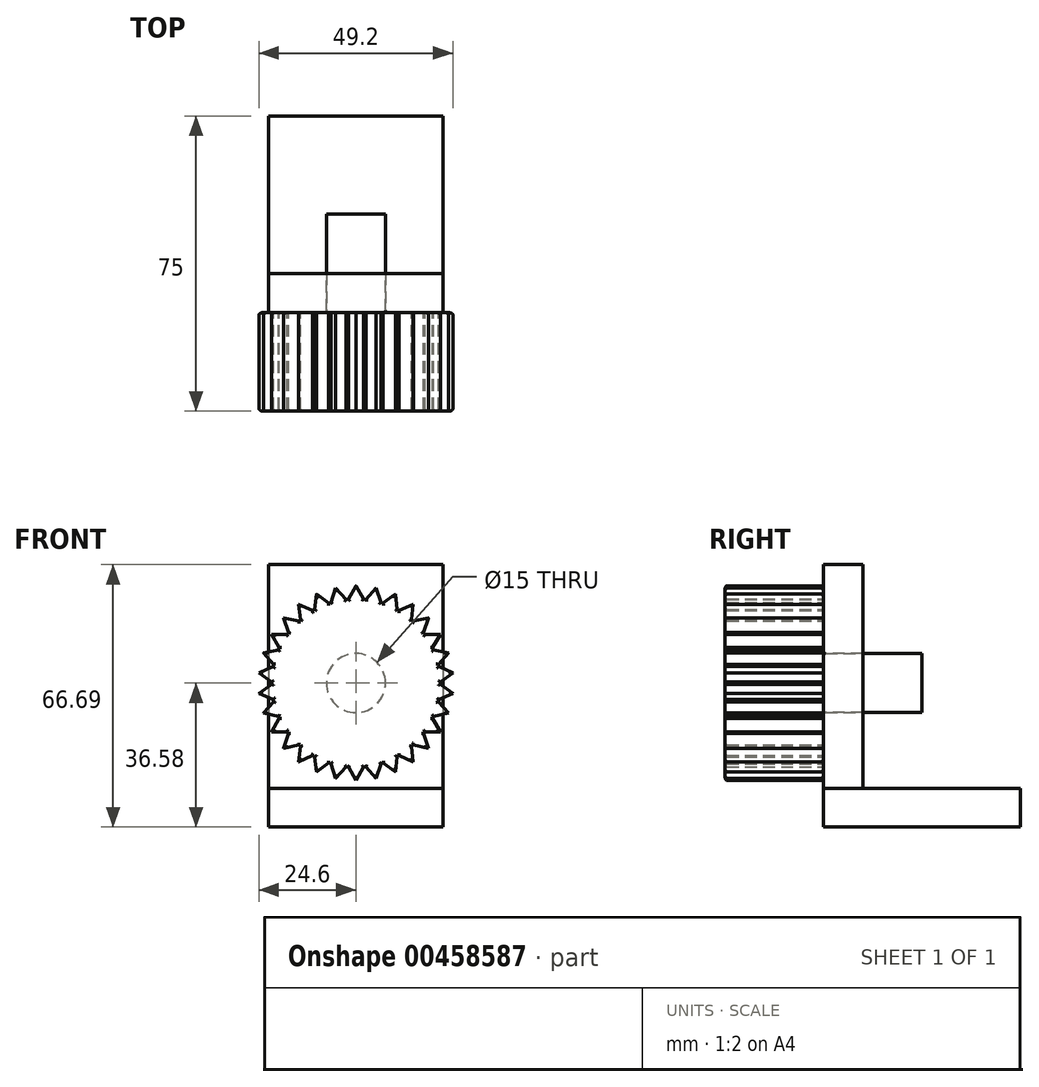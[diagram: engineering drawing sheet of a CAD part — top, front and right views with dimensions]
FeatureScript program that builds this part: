
annotation { "Feature Type Name" : "Feature", "Feature Type Description" : "" }
export const myFeature = defineFeature(function(context is Context, id is Id, definition is map)
    precondition{}
    {
        {
            var Q0;
            Q0=qCreatedBy(makeId("Front.planeOp"),FACE);
            var sketch = newSketch(context, id + "F0", { "sketchPlane" : qUnion([Q0])});
            skLineSegment(sketch, "E0.1", {"start": v(-1.94, 21.37) * mm, "end": v(0, 24.73) * mm});
            skLineSegment(sketch, "E0.2", {"start": v(0, 24.73) * mm, "end": v(1.94, 21.37) * mm});
            skLineSegment(sketch, "E1.1.0", {"start": v(-5.14, 24.2) * mm, "end": v(-2.54, 21.3) * mm});
            skLineSegment(sketch, "E1.1.1", {"start": v(-6.34, 20.5) * mm, "end": v(-5.14, 24.2) * mm});
            skLineSegment(sketch, "E1.2.0", {"start": v(-10.06, 22.6) * mm, "end": v(-6.91, 20.3) * mm});
            skLineSegment(sketch, "E1.2.1", {"start": v(-10.47, 18.73) * mm, "end": v(-10.06, 22.6) * mm});
            skPoint(sketch, "E1.center", {"position": v(0, 0) * mm});
            skLineSegment(sketch, "E2.3.3.0", {"start": v(-14.13, 16.14) * mm, "end": v(-14.54, 20.01) * mm});
            skLineSegment(sketch, "E2.4.3.0", {"start": v(-14.54, 20.01) * mm, "end": v(-10.99, 18.43) * mm});
            skLineSegment(sketch, "E2.3.4.0", {"start": v(-17.18, 12.85) * mm, "end": v(-18.38, 16.55) * mm});
            skLineSegment(sketch, "E2.4.4.0", {"start": v(-18.38, 16.55) * mm, "end": v(-14.58, 15.74) * mm});
            skLineSegment(sketch, "E2.3.5.0", {"start": v(-19.48, 9) * mm, "end": v(-21.42, 12.37) * mm});
            skLineSegment(sketch, "E2.4.5.0", {"start": v(-21.42, 12.37) * mm, "end": v(-17.53, 12.37) * mm});
            skLineSegment(sketch, "E2.3.6.0", {"start": v(-20.92, 4.75) * mm, "end": v(-23.52, 7.64) * mm});
            skLineSegment(sketch, "E2.4.6.0", {"start": v(-23.52, 7.64) * mm, "end": v(-19.72, 8.45) * mm});
            skLineSegment(sketch, "E2.3.7.0", {"start": v(-21.45, 0.3) * mm, "end": v(-24.6, 2.59) * mm});
            skLineSegment(sketch, "E2.4.7.0", {"start": v(-24.6, 2.59) * mm, "end": v(-21.05, 4.17) * mm});
            skLineSegment(sketch, "E2.3.8.0", {"start": v(-21.05, -4.17) * mm, "end": v(-24.6, -2.59) * mm});
            skLineSegment(sketch, "E2.4.8.0", {"start": v(-24.6, -2.59) * mm, "end": v(-21.45, -0.3) * mm});
            skLineSegment(sketch, "E2.3.9.0", {"start": v(-19.72, -8.45) * mm, "end": v(-23.52, -7.64) * mm});
            skLineSegment(sketch, "E2.4.9.0", {"start": v(-23.52, -7.64) * mm, "end": v(-20.92, -4.75) * mm});
            skLineSegment(sketch, "E2.3.10.0", {"start": v(-17.53, -12.37) * mm, "end": v(-21.42, -12.37) * mm});
            skLineSegment(sketch, "E2.4.10.0", {"start": v(-21.42, -12.37) * mm, "end": v(-19.48, -9) * mm});
            skLineSegment(sketch, "E2.3.11.0", {"start": v(-14.58, -15.74) * mm, "end": v(-18.38, -16.55) * mm});
            skLineSegment(sketch, "E2.4.11.0", {"start": v(-18.38, -16.55) * mm, "end": v(-17.18, -12.85) * mm});
            skLineSegment(sketch, "E2.3.12.0", {"start": v(-10.99, -18.43) * mm, "end": v(-14.54, -20.01) * mm});
            skLineSegment(sketch, "E2.4.12.0", {"start": v(-14.54, -20.01) * mm, "end": v(-14.13, -16.14) * mm});
            skLineSegment(sketch, "E2.3.13.0", {"start": v(-6.91, -20.3) * mm, "end": v(-10.06, -22.6) * mm});
            skLineSegment(sketch, "E2.4.13.0", {"start": v(-10.06, -22.6) * mm, "end": v(-10.47, -18.73) * mm});
            skLineSegment(sketch, "E2.3.14.0", {"start": v(-2.54, -21.3) * mm, "end": v(-5.14, -24.2) * mm});
            skLineSegment(sketch, "E2.4.14.0", {"start": v(-5.14, -24.2) * mm, "end": v(-6.34, -20.5) * mm});
            skLineSegment(sketch, "E2.3.15.0", {"start": v(1.94, -21.37) * mm, "end": v(0, -24.73) * mm});
            skLineSegment(sketch, "E2.4.15.0", {"start": v(0, -24.73) * mm, "end": v(-1.94, -21.37) * mm});
            skLineSegment(sketch, "E2.3.16.0", {"start": v(6.34, -20.5) * mm, "end": v(5.14, -24.2) * mm});
            skLineSegment(sketch, "E2.4.16.0", {"start": v(5.14, -24.2) * mm, "end": v(2.54, -21.3) * mm});
            skLineSegment(sketch, "E2.3.17.0", {"start": v(10.47, -18.73) * mm, "end": v(10.06, -22.6) * mm});
            skLineSegment(sketch, "E2.4.17.0", {"start": v(10.06, -22.6) * mm, "end": v(6.91, -20.3) * mm});
            skLineSegment(sketch, "E2.3.18.0", {"start": v(14.13, -16.14) * mm, "end": v(14.54, -20.01) * mm});
            skLineSegment(sketch, "E2.4.18.0", {"start": v(14.54, -20.01) * mm, "end": v(10.99, -18.43) * mm});
            skLineSegment(sketch, "E2.3.19.0", {"start": v(17.18, -12.85) * mm, "end": v(18.38, -16.55) * mm});
            skLineSegment(sketch, "E2.4.19.0", {"start": v(18.38, -16.55) * mm, "end": v(14.58, -15.74) * mm});
            skLineSegment(sketch, "E2.3.20.0", {"start": v(19.48, -9) * mm, "end": v(21.42, -12.37) * mm});
            skLineSegment(sketch, "E2.4.20.0", {"start": v(21.42, -12.37) * mm, "end": v(17.53, -12.37) * mm});
            skLineSegment(sketch, "E2.3.21.0", {"start": v(20.92, -4.75) * mm, "end": v(23.52, -7.64) * mm});
            skLineSegment(sketch, "E2.4.21.0", {"start": v(23.52, -7.64) * mm, "end": v(19.72, -8.45) * mm});
            skLineSegment(sketch, "E2.3.22.0", {"start": v(21.45, -0.3) * mm, "end": v(24.6, -2.59) * mm});
            skLineSegment(sketch, "E2.4.22.0", {"start": v(24.6, -2.59) * mm, "end": v(21.05, -4.17) * mm});
            skLineSegment(sketch, "E2.3.23.0", {"start": v(21.05, 4.17) * mm, "end": v(24.6, 2.59) * mm});
            skLineSegment(sketch, "E2.4.23.0", {"start": v(24.6, 2.59) * mm, "end": v(21.45, 0.3) * mm});
            skLineSegment(sketch, "E2.3.24.0", {"start": v(19.72, 8.45) * mm, "end": v(23.52, 7.64) * mm});
            skLineSegment(sketch, "E2.4.24.0", {"start": v(23.52, 7.64) * mm, "end": v(20.92, 4.75) * mm});
            skLineSegment(sketch, "E2.3.25.0", {"start": v(17.53, 12.37) * mm, "end": v(21.42, 12.37) * mm});
            skLineSegment(sketch, "E2.4.25.0", {"start": v(21.42, 12.37) * mm, "end": v(19.48, 9) * mm});
            skLineSegment(sketch, "E2.3.26.0", {"start": v(14.58, 15.74) * mm, "end": v(18.38, 16.55) * mm});
            skLineSegment(sketch, "E2.4.26.0", {"start": v(18.38, 16.55) * mm, "end": v(17.18, 12.85) * mm});
            skLineSegment(sketch, "E2.3.27.0", {"start": v(10.99, 18.43) * mm, "end": v(14.54, 20.01) * mm});
            skLineSegment(sketch, "E2.4.27.0", {"start": v(14.54, 20.01) * mm, "end": v(14.13, 16.14) * mm});
            skLineSegment(sketch, "E2.3.28.0", {"start": v(6.91, 20.3) * mm, "end": v(10.06, 22.6) * mm});
            skLineSegment(sketch, "E2.4.28.0", {"start": v(10.06, 22.6) * mm, "end": v(10.47, 18.73) * mm});
            skLineSegment(sketch, "E2.3.29.0", {"start": v(2.54, 21.3) * mm, "end": v(5.14, 24.2) * mm});
            skLineSegment(sketch, "E2.4.29.0", {"start": v(5.14, 24.2) * mm, "end": v(6.34, 20.5) * mm});
            skLineSegment(sketch, "E3", {"start": v(-2.54, 21.3) * mm, "end": v(-1.94, 21.37) * mm});
            skLineSegment(sketch, "E4.1.0", {"start": v(-6.91, 20.3) * mm, "end": v(-6.34, 20.5) * mm});
            skLineSegment(sketch, "E4.2.0", {"start": v(-10.99, 18.43) * mm, "end": v(-10.47, 18.73) * mm});
            skLineSegment(sketch, "E4.3.0", {"start": v(-14.58, 15.74) * mm, "end": v(-14.13, 16.14) * mm});
            skLineSegment(sketch, "E4.4.0", {"start": v(-17.53, 12.37) * mm, "end": v(-17.18, 12.85) * mm});
            skLineSegment(sketch, "E4.5.0", {"start": v(-19.72, 8.45) * mm, "end": v(-19.48, 9) * mm});
            skLineSegment(sketch, "E4.6.0", {"start": v(-21.05, 4.17) * mm, "end": v(-20.92, 4.75) * mm});
            skLineSegment(sketch, "E4.7.0", {"start": v(-21.45, -0.3) * mm, "end": v(-21.45, 0.3) * mm});
            skLineSegment(sketch, "E4.8.0", {"start": v(-20.92, -4.75) * mm, "end": v(-21.05, -4.17) * mm});
            skLineSegment(sketch, "E4.9.0", {"start": v(-19.48, -9) * mm, "end": v(-19.72, -8.45) * mm});
            skLineSegment(sketch, "E4.10.0", {"start": v(-17.18, -12.85) * mm, "end": v(-17.53, -12.37) * mm});
            skLineSegment(sketch, "E4.11.0", {"start": v(-14.13, -16.14) * mm, "end": v(-14.58, -15.74) * mm});
            skLineSegment(sketch, "E4.12.0", {"start": v(-10.47, -18.73) * mm, "end": v(-10.99, -18.43) * mm});
            skLineSegment(sketch, "E4.13.0", {"start": v(-6.34, -20.5) * mm, "end": v(-6.91, -20.3) * mm});
            skLineSegment(sketch, "E4.14.0", {"start": v(-1.94, -21.37) * mm, "end": v(-2.54, -21.3) * mm});
            skLineSegment(sketch, "E4.15.0", {"start": v(2.54, -21.3) * mm, "end": v(1.94, -21.37) * mm});
            skLineSegment(sketch, "E4.16.0", {"start": v(6.91, -20.3) * mm, "end": v(6.34, -20.5) * mm});
            skLineSegment(sketch, "E4.17.0", {"start": v(10.99, -18.43) * mm, "end": v(10.47, -18.73) * mm});
            skLineSegment(sketch, "E4.18.0", {"start": v(14.58, -15.74) * mm, "end": v(14.13, -16.14) * mm});
            skLineSegment(sketch, "E4.19.0", {"start": v(17.53, -12.37) * mm, "end": v(17.18, -12.85) * mm});
            skLineSegment(sketch, "E4.20.0", {"start": v(19.72, -8.45) * mm, "end": v(19.48, -9) * mm});
            skLineSegment(sketch, "E4.21.0", {"start": v(21.05, -4.17) * mm, "end": v(20.92, -4.75) * mm});
            skLineSegment(sketch, "E4.22.0", {"start": v(21.45, 0.3) * mm, "end": v(21.45, -0.3) * mm});
            skLineSegment(sketch, "E4.23.0", {"start": v(20.92, 4.75) * mm, "end": v(21.05, 4.17) * mm});
            skLineSegment(sketch, "E4.24.0", {"start": v(19.48, 9) * mm, "end": v(19.72, 8.45) * mm});
            skLineSegment(sketch, "E4.25.0", {"start": v(17.18, 12.85) * mm, "end": v(17.53, 12.37) * mm});
            skLineSegment(sketch, "E4.26.0", {"start": v(14.13, 16.14) * mm, "end": v(14.58, 15.74) * mm});
            skLineSegment(sketch, "E4.27.0", {"start": v(10.47, 18.73) * mm, "end": v(10.99, 18.43) * mm});
            skLineSegment(sketch, "E4.28.0", {"start": v(6.34, 20.5) * mm, "end": v(6.91, 20.3) * mm});
            skLineSegment(sketch, "E4.29.0", {"start": v(1.94, 21.37) * mm, "end": v(2.54, 21.3) * mm});
            skCircle(sketch, "E5", {"center": v(0, 0) * mm, "radius": 7.5 * mm});
            skSolve(sketch);
        }
        {
            var Q0;
            Q0=makeQuery(id+"F0.imprint","IMPRINT",FACE,{"disambiguationData":[TD([[makeQuery(id+"F0.imprint","IMPRINT",EDGE,{"derivedFrom":sQuery(id+"F0.wireOp",EDGE,"E0.1")}),-1.0]])]});
            extrude(context, id + "F1", {"entities" : qUnion([Q0]), "depth" : 25 * mm});
        }
        {
            var Q0;
            Q0=makeQuery(id+"F0.imprint","IMPRINT",FACE,{"disambiguationData":[TD([[makeQuery(id+"F0.imprint","IMPRINT",EDGE,{"derivedFrom":sQuery(id+"F0.wireOp",EDGE,"E5")}),1.0]])]});
            extrude(context, id + "F2", {"entities" : qUnion([Q0]), "operationType" : NewBodyOperationType.ADD, "endBound" : BoundingType.SYMMETRIC, "depth" : 50 * mm});
        }
        {
            var Q0;
            {var subQ0=sQuery(id+"F0.wireOp",EDGE,"E5");Q0=makeQuery(id+"F2.boolean.opBoolean","MERGE",FACE,{"derivedFrom":[makeQuery(id+"F1.opExtrude","CAP_FACE",FACE,{"disambiguationData":[OSD([sQuery(id+"F0.wireOp",EDGE,"E0.1"),sQuery(id+"F0.wireOp",EDGE,"E0.2"),sQuery(id+"F0.wireOp",EDGE,"E1.1.0"),sQuery(id+"F0.wireOp",EDGE,"E1.1.1"),sQuery(id+"F0.wireOp",EDGE,"E1.2.0"),sQuery(id+"F0.wireOp",EDGE,"E1.2.1"),sQuery(id+"F0.wireOp",EDGE,"E2.3.3.0"),sQuery(id+"F0.wireOp",EDGE,"E2.4.3.0"),sQuery(id+"F0.wireOp",EDGE,"E2.3.4.0"),sQuery(id+"F0.wireOp",EDGE,"E2.4.4.0"),sQuery(id+"F0.wireOp",EDGE,"E2.3.5.0"),sQuery(id+"F0.wireOp",EDGE,"E2.4.5.0"),sQuery(id+"F0.wireOp",EDGE,"E2.3.6.0"),sQuery(id+"F0.wireOp",EDGE,"E2.4.6.0"),sQuery(id+"F0.wireOp",EDGE,"E2.3.7.0"),sQuery(id+"F0.wireOp",EDGE,"E2.4.7.0"),sQuery(id+"F0.wireOp",EDGE,"E2.3.8.0"),sQuery(id+"F0.wireOp",EDGE,"E2.4.8.0"),sQuery(id+"F0.wireOp",EDGE,"E2.3.9.0"),sQuery(id+"F0.wireOp",EDGE,"E2.4.9.0"),sQuery(id+"F0.wireOp",EDGE,"E2.3.10.0"),sQuery(id+"F0.wireOp",EDGE,"E2.4.10.0"),sQuery(id+"F0.wireOp",EDGE,"E2.3.11.0"),sQuery(id+"F0.wireOp",EDGE,"E2.4.11.0"),sQuery(id+"F0.wireOp",EDGE,"E2.3.12.0"),sQuery(id+"F0.wireOp",EDGE,"E2.4.12.0"),sQuery(id+"F0.wireOp",EDGE,"E2.3.13.0"),sQuery(id+"F0.wireOp",EDGE,"E2.4.13.0"),sQuery(id+"F0.wireOp",EDGE,"E2.3.14.0"),sQuery(id+"F0.wireOp",EDGE,"E2.4.14.0"),sQuery(id+"F0.wireOp",EDGE,"E2.3.15.0"),sQuery(id+"F0.wireOp",EDGE,"E2.4.15.0"),sQuery(id+"F0.wireOp",EDGE,"E2.3.16.0"),sQuery(id+"F0.wireOp",EDGE,"E2.4.16.0"),sQuery(id+"F0.wireOp",EDGE,"E2.3.17.0"),sQuery(id+"F0.wireOp",EDGE,"E2.4.17.0"),sQuery(id+"F0.wireOp",EDGE,"E2.3.18.0"),sQuery(id+"F0.wireOp",EDGE,"E2.4.18.0"),sQuery(id+"F0.wireOp",EDGE,"E2.3.19.0"),sQuery(id+"F0.wireOp",EDGE,"E2.4.19.0"),sQuery(id+"F0.wireOp",EDGE,"E2.3.20.0"),sQuery(id+"F0.wireOp",EDGE,"E2.4.20.0"),sQuery(id+"F0.wireOp",EDGE,"E2.3.21.0"),sQuery(id+"F0.wireOp",EDGE,"E2.4.21.0"),sQuery(id+"F0.wireOp",EDGE,"E2.3.22.0"),sQuery(id+"F0.wireOp",EDGE,"E2.4.22.0"),sQuery(id+"F0.wireOp",EDGE,"E2.3.23.0"),sQuery(id+"F0.wireOp",EDGE,"E2.4.23.0"),sQuery(id+"F0.wireOp",EDGE,"E2.3.24.0"),sQuery(id+"F0.wireOp",EDGE,"E2.4.24.0"),sQuery(id+"F0.wireOp",EDGE,"E2.3.25.0"),sQuery(id+"F0.wireOp",EDGE,"E2.4.25.0"),sQuery(id+"F0.wireOp",EDGE,"E2.3.26.0"),sQuery(id+"F0.wireOp",EDGE,"E2.4.26.0"),sQuery(id+"F0.wireOp",EDGE,"E2.3.27.0"),sQuery(id+"F0.wireOp",EDGE,"E2.4.27.0"),sQuery(id+"F0.wireOp",EDGE,"E2.3.28.0"),sQuery(id+"F0.wireOp",EDGE,"E2.4.28.0"),sQuery(id+"F0.wireOp",EDGE,"E2.3.29.0"),sQuery(id+"F0.wireOp",EDGE,"E2.4.29.0"),sQuery(id+"F0.wireOp",EDGE,"E3"),sQuery(id+"F0.wireOp",EDGE,"E4.1.0"),sQuery(id+"F0.wireOp",EDGE,"E4.2.0"),sQuery(id+"F0.wireOp",EDGE,"E4.3.0"),sQuery(id+"F0.wireOp",EDGE,"E4.4.0"),sQuery(id+"F0.wireOp",EDGE,"E4.5.0"),sQuery(id+"F0.wireOp",EDGE,"E4.6.0"),sQuery(id+"F0.wireOp",EDGE,"E4.7.0"),sQuery(id+"F0.wireOp",EDGE,"E4.8.0"),sQuery(id+"F0.wireOp",EDGE,"E4.9.0"),sQuery(id+"F0.wireOp",EDGE,"E4.10.0"),sQuery(id+"F0.wireOp",EDGE,"E4.11.0"),sQuery(id+"F0.wireOp",EDGE,"E4.12.0"),sQuery(id+"F0.wireOp",EDGE,"E4.13.0"),sQuery(id+"F0.wireOp",EDGE,"E4.14.0"),sQuery(id+"F0.wireOp",EDGE,"E4.15.0"),sQuery(id+"F0.wireOp",EDGE,"E4.16.0"),sQuery(id+"F0.wireOp",EDGE,"E4.17.0"),sQuery(id+"F0.wireOp",EDGE,"E4.18.0"),sQuery(id+"F0.wireOp",EDGE,"E4.19.0"),sQuery(id+"F0.wireOp",EDGE,"E4.20.0"),sQuery(id+"F0.wireOp",EDGE,"E4.21.0"),sQuery(id+"F0.wireOp",EDGE,"E4.22.0"),sQuery(id+"F0.wireOp",EDGE,"E4.23.0"),sQuery(id+"F0.wireOp",EDGE,"E4.24.0"),sQuery(id+"F0.wireOp",EDGE,"E4.25.0"),sQuery(id+"F0.wireOp",EDGE,"E4.26.0"),sQuery(id+"F0.wireOp",EDGE,"E4.27.0"),sQuery(id+"F0.wireOp",EDGE,"E4.28.0"),sQuery(id+"F0.wireOp",EDGE,"E4.29.0"),subQ0])],"isStart":false}),makeQuery(id+"F2.opExtrude","CAP_FACE",FACE,{"disambiguationData":[OSD([subQ0])],"isStart":false})]});}
            var Q1;
            Q1=makeQuery(id+"F1.opExtrude","CAP_EDGE",EDGE,{"disambiguationData":[OSD([sQuery(id+"F0.wireOp",EDGE,"E2.4.9.0")])],"isStart":false});
            fillet(context, id + "F3", {"entities" : qUnion([Q0, Q1]), "radius" : 0.5 * mm, "tangentPropagation" : true, "allowEdgeOverflow" : false});
        }
        {
            var Q0;
            Q0=makeQuery(id+"F1.opExtrude","CAP_EDGE",EDGE,{"disambiguationData":[OSD([sQuery(id+"F0.wireOp",EDGE,"E1.2.1")])],"isStart":true});
            var Q1;
            Q1=makeQuery(id+"F1.opExtrude","CAP_FACE",FACE,{"disambiguationData":[OSD([sQuery(id+"F0.wireOp",EDGE,"E0.1"),sQuery(id+"F0.wireOp",EDGE,"E0.2"),sQuery(id+"F0.wireOp",EDGE,"E1.1.0"),sQuery(id+"F0.wireOp",EDGE,"E1.1.1"),sQuery(id+"F0.wireOp",EDGE,"E1.2.0"),sQuery(id+"F0.wireOp",EDGE,"E1.2.1"),sQuery(id+"F0.wireOp",EDGE,"E2.3.3.0"),sQuery(id+"F0.wireOp",EDGE,"E2.4.3.0"),sQuery(id+"F0.wireOp",EDGE,"E2.3.4.0"),sQuery(id+"F0.wireOp",EDGE,"E2.4.4.0"),sQuery(id+"F0.wireOp",EDGE,"E2.3.5.0"),sQuery(id+"F0.wireOp",EDGE,"E2.4.5.0"),sQuery(id+"F0.wireOp",EDGE,"E2.3.6.0"),sQuery(id+"F0.wireOp",EDGE,"E2.4.6.0"),sQuery(id+"F0.wireOp",EDGE,"E2.3.7.0"),sQuery(id+"F0.wireOp",EDGE,"E2.4.7.0"),sQuery(id+"F0.wireOp",EDGE,"E2.3.8.0"),sQuery(id+"F0.wireOp",EDGE,"E2.4.8.0"),sQuery(id+"F0.wireOp",EDGE,"E2.3.9.0"),sQuery(id+"F0.wireOp",EDGE,"E2.4.9.0"),sQuery(id+"F0.wireOp",EDGE,"E2.3.10.0"),sQuery(id+"F0.wireOp",EDGE,"E2.4.10.0"),sQuery(id+"F0.wireOp",EDGE,"E2.3.11.0"),sQuery(id+"F0.wireOp",EDGE,"E2.4.11.0"),sQuery(id+"F0.wireOp",EDGE,"E2.3.12.0"),sQuery(id+"F0.wireOp",EDGE,"E2.4.12.0"),sQuery(id+"F0.wireOp",EDGE,"E2.3.13.0"),sQuery(id+"F0.wireOp",EDGE,"E2.4.13.0"),sQuery(id+"F0.wireOp",EDGE,"E2.3.14.0"),sQuery(id+"F0.wireOp",EDGE,"E2.4.14.0"),sQuery(id+"F0.wireOp",EDGE,"E2.3.15.0"),sQuery(id+"F0.wireOp",EDGE,"E2.4.15.0"),sQuery(id+"F0.wireOp",EDGE,"E2.3.16.0"),sQuery(id+"F0.wireOp",EDGE,"E2.4.16.0"),sQuery(id+"F0.wireOp",EDGE,"E2.3.17.0"),sQuery(id+"F0.wireOp",EDGE,"E2.4.17.0"),sQuery(id+"F0.wireOp",EDGE,"E2.3.18.0"),sQuery(id+"F0.wireOp",EDGE,"E2.4.18.0"),sQuery(id+"F0.wireOp",EDGE,"E2.3.19.0"),sQuery(id+"F0.wireOp",EDGE,"E2.4.19.0"),sQuery(id+"F0.wireOp",EDGE,"E2.3.20.0"),sQuery(id+"F0.wireOp",EDGE,"E2.4.20.0"),sQuery(id+"F0.wireOp",EDGE,"E2.3.21.0"),sQuery(id+"F0.wireOp",EDGE,"E2.4.21.0"),sQuery(id+"F0.wireOp",EDGE,"E2.3.22.0"),sQuery(id+"F0.wireOp",EDGE,"E2.4.22.0"),sQuery(id+"F0.wireOp",EDGE,"E2.3.23.0"),sQuery(id+"F0.wireOp",EDGE,"E2.4.23.0"),sQuery(id+"F0.wireOp",EDGE,"E2.3.24.0"),sQuery(id+"F0.wireOp",EDGE,"E2.4.24.0"),sQuery(id+"F0.wireOp",EDGE,"E2.3.25.0"),sQuery(id+"F0.wireOp",EDGE,"E2.4.25.0"),sQuery(id+"F0.wireOp",EDGE,"E2.3.26.0"),sQuery(id+"F0.wireOp",EDGE,"E2.4.26.0"),sQuery(id+"F0.wireOp",EDGE,"E2.3.27.0"),sQuery(id+"F0.wireOp",EDGE,"E2.4.27.0"),sQuery(id+"F0.wireOp",EDGE,"E2.3.28.0"),sQuery(id+"F0.wireOp",EDGE,"E2.4.28.0"),sQuery(id+"F0.wireOp",EDGE,"E2.3.29.0"),sQuery(id+"F0.wireOp",EDGE,"E2.4.29.0"),sQuery(id+"F0.wireOp",EDGE,"E3"),sQuery(id+"F0.wireOp",EDGE,"E4.1.0"),sQuery(id+"F0.wireOp",EDGE,"E4.2.0"),sQuery(id+"F0.wireOp",EDGE,"E4.3.0"),sQuery(id+"F0.wireOp",EDGE,"E4.4.0"),sQuery(id+"F0.wireOp",EDGE,"E4.5.0"),sQuery(id+"F0.wireOp",EDGE,"E4.6.0"),sQuery(id+"F0.wireOp",EDGE,"E4.7.0"),sQuery(id+"F0.wireOp",EDGE,"E4.8.0"),sQuery(id+"F0.wireOp",EDGE,"E4.9.0"),sQuery(id+"F0.wireOp",EDGE,"E4.10.0"),sQuery(id+"F0.wireOp",EDGE,"E4.11.0"),sQuery(id+"F0.wireOp",EDGE,"E4.12.0"),sQuery(id+"F0.wireOp",EDGE,"E4.13.0"),sQuery(id+"F0.wireOp",EDGE,"E4.14.0"),sQuery(id+"F0.wireOp",EDGE,"E4.15.0"),sQuery(id+"F0.wireOp",EDGE,"E4.16.0"),sQuery(id+"F0.wireOp",EDGE,"E4.17.0"),sQuery(id+"F0.wireOp",EDGE,"E4.18.0"),sQuery(id+"F0.wireOp",EDGE,"E4.19.0"),sQuery(id+"F0.wireOp",EDGE,"E4.20.0"),sQuery(id+"F0.wireOp",EDGE,"E4.21.0"),sQuery(id+"F0.wireOp",EDGE,"E4.22.0"),sQuery(id+"F0.wireOp",EDGE,"E4.23.0"),sQuery(id+"F0.wireOp",EDGE,"E4.24.0"),sQuery(id+"F0.wireOp",EDGE,"E4.25.0"),sQuery(id+"F0.wireOp",EDGE,"E4.26.0"),sQuery(id+"F0.wireOp",EDGE,"E4.27.0"),sQuery(id+"F0.wireOp",EDGE,"E4.28.0"),sQuery(id+"F0.wireOp",EDGE,"E4.29.0"),sQuery(id+"F0.wireOp",EDGE,"E5")])],"isStart":true});
            fillet(context, id + "F4", {"entities" : qUnion([Q0, Q1]), "radius" : 0.5 * mm, "tangentPropagation" : true, "allowEdgeOverflow" : false});
        }
        {
            var Q0;
            Q0=qCreatedBy(makeId("Front.planeOp"),FACE);
            var sketch = newSketch(context, id + "F5", { "sketchPlane" : qUnion([Q0])});
            skLineSegment(sketch, "E6.bottom", {"start": v(-22.17, 30.11) * mm, "end": v(22.17, 30.11) * mm});
            skLineSegment(sketch, "E6.top", {"start": v(-22.17, -36.58) * mm, "end": v(22.17, -36.58) * mm});
            skLineSegment(sketch, "E6.left", {"start": v(-22.17, 30.11) * mm, "end": v(-22.17, -36.58) * mm});
            skLineSegment(sketch, "E6.right", {"start": v(22.17, 30.11) * mm, "end": v(22.17, -36.58) * mm});
            skLineSegment(sketch, "E7.top", {"start": v(-22.17, -26.7) * mm, "end": v(22.17, -26.7) * mm});
            skLineSegment(sketch, "E7.left", {"start": v(-22.17, -36.58) * mm, "end": v(-22.17, -26.7) * mm});
            skLineSegment(sketch, "E7.right", {"start": v(22.17, -36.58) * mm, "end": v(22.17, -26.7) * mm});
            skCircle(sketch, "E8", {"center": v(0, 0) * mm, "radius": 7.5 * mm});
            skSolve(sketch);
        }
        {
            var Q0;
            Q0=makeQuery(id+"F5.imprint","IMPRINT",FACE,{"disambiguationData":[TD([[makeQuery(id+"F5.imprint","IMPRINT",EDGE,{"derivedFrom":sQuery(id+"F5.wireOp",EDGE,"E6.top")}),1.0]])]});
            extrude(context, id + "F6", {"entities" : qUnion([Q0]), "depth" : -50 * mm});
        }
        {
            var Q0;
            Q0=makeQuery(id+"F5.imprint","IMPRINT",FACE,{"disambiguationData":[TD([[makeQuery(id+"F5.imprint","IMPRINT",EDGE,{"derivedFrom":sQuery(id+"F5.wireOp",EDGE,"E6.bottom")}),-1.0]])]});
            extrude(context, id + "F7", {"entities" : qUnion([Q0]), "depth" : -10 * mm});
        }
    });
